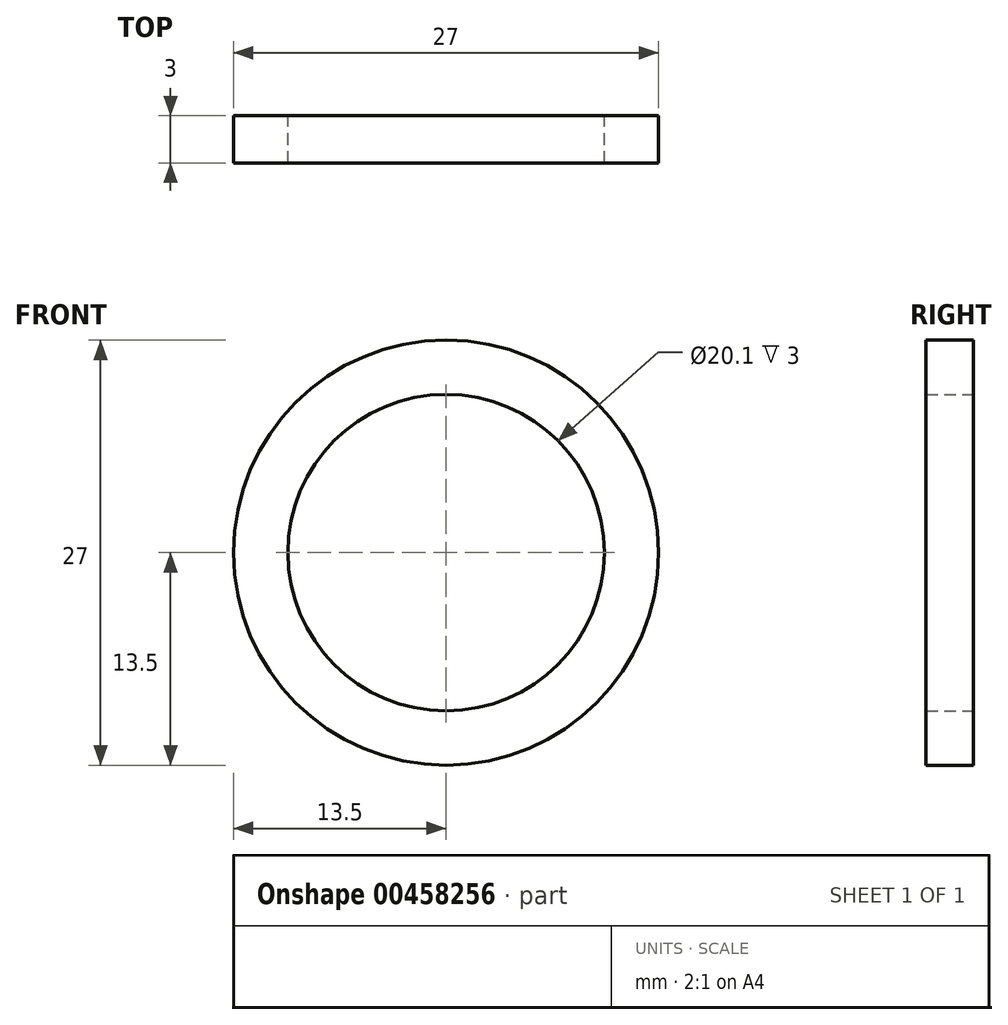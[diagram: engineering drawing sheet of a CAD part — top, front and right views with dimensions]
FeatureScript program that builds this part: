
annotation { "Feature Type Name" : "Feature", "Feature Type Description" : "" }
export const myFeature = defineFeature(function(context is Context, id is Id, definition is map)
    precondition{}
    {
        {
            var Q0;
            Q0=qCreatedBy(makeId("Front.planeOp"),FACE);
            var sketch = newSketch(context, id + "F0", { "sketchPlane" : qUnion([Q0])});
            skCircle(sketch, "E0", {"center": v(0, 0) * mm, "radius": 13.5 * mm});
            skCircle(sketch, "E1", {"center": v(0, 0) * mm, "radius": 10.05 * mm});
            skSolve(sketch);
        }
        {
            var Q0;
            Q0=makeQuery(id+"F0.imprint","IMPRINT",FACE,{"disambiguationData":[TD([[makeQuery(id+"F0.imprint","IMPRINT",EDGE,{"derivedFrom":sQuery(id+"F0.wireOp",EDGE,"E0")}),1.0]])]});
            extrude(context, id + "F1", {"entities" : qUnion([Q0]), "depth" : 3 * mm});
        }
    });
